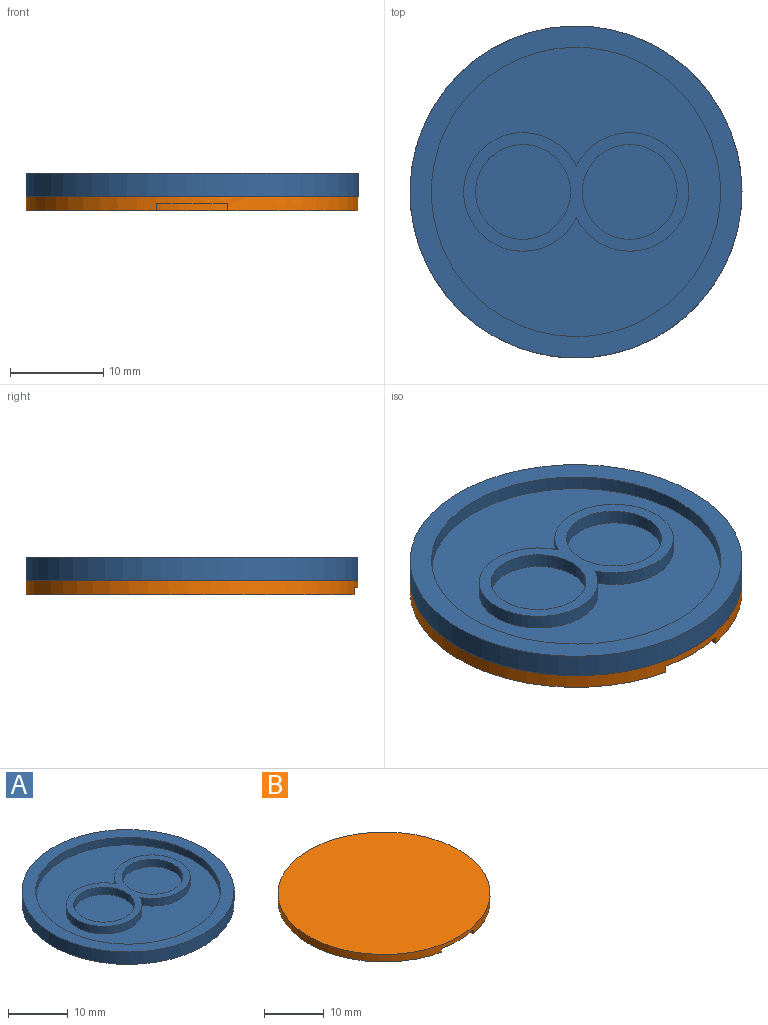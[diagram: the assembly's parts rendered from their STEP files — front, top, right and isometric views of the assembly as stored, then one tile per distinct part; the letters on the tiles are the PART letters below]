
ASSEMBLY  parts=2 mates=1
PART A: 12 faces, bbox 35.6x35.6x2.5 mm
  f0: cylinder r=17.78mm len=35.56mm, axis (0,0,-1), area 283.8mm2, adj f1,f2
  f1: plane 35.56x35.56mm, normal (0,0,1), area 239mm2, adj f0,f3
  f2: plane 35.56x35.56mm, normal (0,0,-1), area 993.1mm2, adj f0
  f3: cylinder r=15.49mm len=30.99mm, axis (0,0,1), area 148.4mm2, adj f1,f4
  f4: plane 30.99x30.99mm, normal (0,0,1), area 505.6mm2, adj f3,f6,f7
  f5: plane 24.13x12.7mm, normal (0,0,1), area 86.5mm2, adj f6,f7,f8,f9
  f6: cylinder r=6.35mm len=12.7mm, axis (0,0,1), area 52.1mm2, adj f4,f5,f7
  f7: cylinder r=6.35mm len=12.7mm, axis (0,0,1), area 52.1mm2, adj f4,f5,f6
  f8: cylinder r=5.08mm len=10.16mm, axis (0,0,1), area 48.6mm2, adj f5,f10
  f9: cylinder r=5.08mm len=10.16mm, axis (0,0,1), area 48.6mm2, adj f5,f11
  f10: plane 10.16x10.16mm, normal (0,0,1), area 81.1mm2, adj f8
  f11: plane 10.16x10.16mm, normal (0,0,1), area 81.1mm2, adj f9
PART B: 170 faces, bbox 35.6x35.6x1.5 mm
  f0: plane 30.99x30.99mm, normal (0,0,-1), area 549.6mm2, adj f4,f5,f6,f7,f8,f9,f10,f11
  f1: plane 35.56x35.15mm, normal (0,0,-1), area 175mm2, adj f2,f165,f167,f169
  f2: cylinder r=17.78mm len=35.56mm, axis (0,0,-1), area 164.4mm2, adj f1,f3,f165,f167,f168
  f3: plane 35.56x35.56mm, normal (0,0,1), area 993.1mm2, adj f2
  f4: plane 1.49x0.76mm, normal (0,-1,0), area 1.1mm2, adj f0,f5,f15,f16
  f5: plane 7.05x0.76mm, normal (-1,0,0), area 5.4mm2, adj f0,f4,f6,f16
  f6: plane 1.49x0.76mm, normal (0,1,0), area 1.1mm2, adj f0,f5,f7,f16
  f7: plane 2.76x0.76mm, normal (1,0,0), area 2.1mm2, adj f0,f6,f8,f16
  f8: plane 2.79x0.76mm, normal (0,1,0), area 2.1mm2, adj f0,f7,f9,f16
  f9: plane 2.76x0.76mm, normal (-1,0,0), area 2.1mm2, adj f0,f8,f10,f16
  f10: plane 1.5x0.76mm, normal (0,1,0), area 1.1mm2, adj f0,f9,f11,f16
  f11: plane 7.05x0.76mm, normal (1,0,0), area 5.4mm2, adj f0,f10,f12,f16
  f12: plane 1.5x0.76mm, normal (0,-1,0), area 1.1mm2, adj f0,f11,f13,f16
  f13: plane 3.04x0.76mm, normal (-1,0,0), area 2.3mm2, adj f0,f12,f14,f16
  f14: plane 2.79x0.76mm, normal (0,-1,0), area 2.1mm2, adj f0,f13,f15,f16
  f15: plane 3.04x0.76mm, normal (1,0,0), area 2.3mm2, adj f0,f4,f14,f16
  f16: plane 7.05x5.78mm, normal (0,0,-1), area 24.5mm2, adj f4,f5,f6,f7,f8,f9,f10,f11
  f17: plane 7.05x0.76mm, normal (-1,0,0), area 5.4mm2, adj f0,f18,f41,f42
  f18: plane 2.19x0.76mm, normal (0,1,0), area 1.7mm2, adj f0,f17,f19,f42
  f19: extruded ~2.18x0.76mm, area 1.7mm2, adj f0,f18,f20,f42
  f20: extruded ~1.36x0.76mm, area 1.2mm2, adj f0,f19,f21,f42
  f21: extruded ~1.04x0.76mm, area 0.8mm2, adj f0,f20,f22,f42
  f22: extruded ~0.79x0.76mm, area 0.7mm2, adj f0,f21,f23,f42
  f23: plane 0.76x0.05mm, normal (1,0,0), area 0mm2, adj f0,f22,f24,f42
  f24: extruded ~0.97x0.76mm, area 0.9mm2, adj f0,f23,f25,f42
  f25: extruded ~1.09x0.76mm, area 0.9mm2, adj f0,f24,f26,f42
  f26: extruded ~1.51x0.76mm, area 1.3mm2, adj f0,f25,f27,f42
  f27: extruded ~1.89x0.76mm, area 1.5mm2, adj f0,f26,f41,f42
  f28: plane 0.93x0.76mm, normal (0,-1,0), area 0.7mm2, adj f29,f39,f42,f44
  f29: plane 1.84x0.76mm, normal (1,0,0), area 1.4mm2, adj f28,f30,f42,f44
  f30: plane 0.97x0.76mm, normal (0,1,0), area 0.7mm2, adj f29,f31,f42,f44
  f31: extruded ~0.91x0.76mm, area 0.7mm2, adj f30,f32,f42,f44
  f32: extruded ~0.76x0.72mm, area 0.6mm2, adj f31,f39,f42,f44
  f33: plane 1.57x0.76mm, normal (1,0,0), area 1.2mm2, adj f34,f40,f42,f43
  f34: plane 0.87x0.76mm, normal (0,1,0), area 0.7mm2, adj f33,f35,f42,f43
  f35: extruded ~0.88x0.76mm, area 0.7mm2, adj f34,f36,f42,f43
  f36: extruded ~0.76x0.62mm, area 0.5mm2, adj f35,f37,f42,f43
  f37: extruded ~0.76x0.58mm, area 0.5mm2, adj f36,f38,f42,f43
  f38: extruded ~0.94x0.76mm, area 0.7mm2, adj f37,f40,f42,f43
  f39: extruded ~1.25x0.88mm, area 1.3mm2, adj f28,f32,f42,f44
  f40: plane 0.79x0.76mm, normal (0,-1,0), area 0.6mm2, adj f33,f38,f42,f43
  f41: plane 2.64x0.76mm, normal (0,-1,0), area 2mm2, adj f0,f17,f27,f42
  f42: plane 7.05x5.23mm, normal (0,0,-1), area 27.1mm2, adj f17,f18,f19,f20,f21,f22,f23,f24
  f43: plane 2.02x1.57mm, normal (0,0,-1), area 2.9mm2, adj f33,f34,f35,f36,f37,f38,f40
  f44: plane 2.18x1.84mm, normal (0,0,-1), area 3.6mm2, adj f28,f29,f30,f31,f32,f39
  f45: extruded ~2.44x2.09mm, area 2.8mm2, adj f0,f46,f52,f53
  f46: extruded ~2.44x2.09mm, area 2.8mm2, adj f0,f45,f47,f53
  f47: extruded ~2.41x2.09mm, area 2.7mm2, adj f0,f46,f52,f53
  f48: extruded ~1.63x1.14mm, area 1.7mm2, adj f49,f51,f53,f54
  f49: extruded ~1.63x1.14mm, area 1.7mm2, adj f48,f50,f53,f54
  f50: extruded ~1.6x1.14mm, area 1.7mm2, adj f49,f51,f53,f54
  f51: extruded ~1.6x1.14mm, area 1.7mm2, adj f48,f50,f53,f54
  f52: extruded ~2.41x2.09mm, area 2.7mm2, adj f0,f45,f47,f53
  f53: plane 4.85x4.18mm, normal (0,0,-1), area 10.4mm2, adj f45,f46,f47,f48,f49,f50,f51,f52
  f54: plane 3.24x2.27mm, normal (0,0,-1), area 6mm2, adj f48,f49,f50,f51
  f55: extruded ~1.45x0.82mm, area 1.3mm2, adj f0,f56,f62,f63
  f56: extruded ~1.6x1.45mm, area 1.9mm2, adj f0,f55,f57,f63
  f57: plane 3.16x0.76mm, normal (-1,0,0), area 2.4mm2, adj f0,f56,f58,f63
  f58: plane 0.93x0.76mm, normal (0,1,0), area 0.7mm2, adj f0,f57,f59,f63
  f59: plane 3.09x0.76mm, normal (1,0,0), area 2.4mm2, adj f0,f58,f60,f63
  f60: extruded ~0.86x0.76mm, area 0.9mm2, adj f0,f59,f61,f63
  f61: extruded ~0.76x0.69mm, area 0.7mm2, adj f0,f60,f62,f63
  f62: plane 0.76x0.64mm, normal (0.59,0.81,0), area 0.6mm2, adj f0,f55,f61,f63
  f63: plane 4.76x2.9mm, normal (0,0,-1), area 5.6mm2, adj f55,f56,f57,f58,f59,f60,f61,f62
  f64: extruded ~2.19x1.82mm, area 2.5mm2, adj f0,f65,f73,f74
  f65: extruded ~2.19x1.81mm, area 2.5mm2, adj f0,f64,f66,f74
  f66: plane 2.57x0.76mm, normal (-1,0,0), area 2mm2, adj f0,f65,f67,f74
  f67: plane 0.9x0.76mm, normal (0,1,0), area 0.7mm2, adj f0,f66,f68,f74
  f68: plane 2.65x0.76mm, normal (1,0,0), area 2mm2, adj f0,f67,f69,f74
  f69: extruded ~1.3x0.91mm, area 1.4mm2, adj f0,f68,f70,f74
  f70: extruded ~1.3x0.88mm, area 1.4mm2, adj f0,f69,f71,f74
  f71: plane 2.65x0.76mm, normal (-1,0,0), area 2mm2, adj f0,f70,f72,f74
  f72: plane 0.93x0.76mm, normal (0,1,0), area 0.7mm2, adj f0,f71,f73,f74
  f73: plane 2.57x0.76mm, normal (1,0,0), area 2mm2, adj f0,f64,f72,f74
  f74: plane 4.76x3.62mm, normal (0,0,-1), area 9.2mm2, adj f64,f65,f66,f67,f68,f69,f70,f71
  f75: plane 4.67x0.76mm, normal (1,0,0), area 3.6mm2, adj f0,f76,f90,f91
  f76: plane 0.88x0.76mm, normal (0,-1,0), area 0.7mm2, adj f0,f75,f77,f91
  f77: plane 1.88x0.76mm, normal (-1,0,0), area 1.4mm2, adj f0,f76,f78,f91
  f78: extruded ~1.63x0.76mm, area 1.2mm2, adj f0,f77,f79,f91
  f79: plane 0.76x0.03mm, normal (0,-1,0), area 0mm2, adj f0,f78,f80,f91
  f80: plane 1x0.76mm, normal (0.9,-0.43,0), area 0.8mm2, adj f0,f79,f81,f91
  f81: plane 2.5x1.35mm, normal (0.88,-0.48,0), area 2.2mm2, adj f0,f80,f82,f91
  f82: plane 0.95x0.76mm, normal (0,-1,0), area 0.7mm2, adj f0,f81,f83,f91
  f83: plane 4.67x0.76mm, normal (-1,0,0), area 3.6mm2, adj f0,f82,f84,f91
  f84: plane 0.88x0.76mm, normal (0,1,0), area 0.7mm2, adj f0,f83,f85,f91
  f85: plane 1.86x0.76mm, normal (1,0,0), area 1.4mm2, adj f0,f84,f86,f91
  f86: extruded ~1.64x0.76mm, area 1.3mm2, adj f0,f85,f87,f91
  f87: plane 0.76x0.03mm, normal (0,1,0), area 0mm2, adj f0,f86,f88,f91
  f88: plane 1.01x0.76mm, normal (-0.91,0.42,0), area 0.8mm2, adj f0,f87,f89,f91
  f89: plane 2.49x1.36mm, normal (-0.88,0.48,0), area 2.2mm2, adj f0,f88,f90,f91
  f90: plane 0.95x0.76mm, normal (0,1,0), area 0.7mm2, adj f0,f75,f89,f91
  f91: plane 4.67x3.57mm, normal (0,0,-1), area 10.9mm2, adj f75,f76,f77,f78,f79,f80,f81,f82
  f92: plane 2.41x1.31mm, normal (0.88,0.48,0), area 2.1mm2, adj f0,f93,f109,f110
  f93: plane 0.99x0.76mm, normal (0,-1,0), area 0.8mm2, adj f0,f92,f94,f110
  f94: plane 1.04x0.76mm, normal (-0.9,-0.43,0), area 0.9mm2, adj f0,f93,f95,f110
  f95: extruded ~0.77x0.76mm, area 0.6mm2, adj f0,f94,f96,f110
  f96: plane 0.76x0.02mm, normal (0,-1,0), area 0mm2, adj f0,f95,f97,f110
  f97: extruded ~0.77x0.76mm, area 0.6mm2, adj f0,f96,f98,f110
  f98: plane 1.04x0.76mm, normal (0.89,-0.45,0), area 0.9mm2, adj f0,f97,f99,f110
  f99: plane 1.04x0.76mm, normal (0,-1,0), area 0.8mm2, adj f0,f98,f100,f110
  f100: plane 2.37x1.31mm, normal (-0.87,0.48,0), area 2.1mm2, adj f0,f99,f101,f110
  f101: plane 2.3x1.23mm, normal (-0.88,-0.47,0), area 2mm2, adj f0,f100,f102,f110
  f102: plane 0.98x0.76mm, normal (0,1,0), area 0.8mm2, adj f0,f101,f103,f110
  f103: plane 0.96x0.76mm, normal (0.91,0.42,0), area 0.8mm2, adj f0,f102,f104,f110
  f104: extruded ~0.76x0.74mm, area 0.6mm2, adj f0,f103,f105,f110
  f105: plane 0.76x0.03mm, normal (0,1,0), area 0mm2, adj f0,f104,f106,f110
  f106: extruded ~0.76x0.74mm, area 0.6mm2, adj f0,f105,f107,f110
  f107: plane 0.96x0.76mm, normal (-0.9,0.44,0), area 0.8mm2, adj f0,f106,f108,f110
  f108: plane 1.04x0.76mm, normal (0,1,0), area 0.8mm2, adj f0,f107,f109,f110
  f109: plane 2.26x1.23mm, normal (0.88,-0.48,0), area 2mm2, adj f0,f92,f108,f110
  f110: plane 4.67x3.78mm, normal (0,0,-1), area 8.4mm2, adj f92,f93,f94,f95,f96,f97,f98,f99
  f111: plane 4.67x0.76mm, normal (1,0,0), area 3.6mm2, adj f0,f112,f114,f115
  f112: plane 0.94x0.76mm, normal (0,-1,0), area 0.7mm2, adj f0,f111,f113,f115
  f113: plane 4.67x0.76mm, normal (-1,0,0), area 3.6mm2, adj f0,f112,f114,f115
  f114: plane 0.94x0.76mm, normal (0,1,0), area 0.7mm2, adj f0,f111,f113,f115
  f115: plane 4.67x0.94mm, normal (0,0,-1), area 4.4mm2, adj f111,f112,f113,f114
  f116: plane 4.67x0.76mm, normal (1,0,0), area 3.6mm2, adj f0,f117,f131,f132
  f117: plane 0.88x0.76mm, normal (0,-1,0), area 0.7mm2, adj f0,f116,f118,f132
  f118: plane 1.88x0.76mm, normal (-1,0,0), area 1.4mm2, adj f0,f117,f119,f132
  f119: extruded ~1.63x0.76mm, area 1.2mm2, adj f0,f118,f120,f132
  f120: plane 0.76x0.03mm, normal (0,-1,0), area 0mm2, adj f0,f119,f121,f132
  f121: plane 1x0.76mm, normal (0.9,-0.43,0), area 0.8mm2, adj f0,f120,f122,f132
  f122: plane 2.5x1.35mm, normal (0.88,-0.48,0), area 2.2mm2, adj f0,f121,f123,f132
  f123: plane 0.95x0.76mm, normal (0,-1,0), area 0.7mm2, adj f0,f122,f124,f132
  f124: plane 4.67x0.76mm, normal (-1,0,0), area 3.6mm2, adj f0,f123,f125,f132
  f125: plane 0.88x0.76mm, normal (0,1,0), area 0.7mm2, adj f0,f124,f126,f132
  f126: plane 1.86x0.76mm, normal (1,0,0), area 1.4mm2, adj f0,f125,f127,f132
  f127: extruded ~1.64x0.76mm, area 1.3mm2, adj f0,f126,f128,f132
  f128: plane 0.76x0.03mm, normal (0,1,0), area 0mm2, adj f0,f127,f129,f132
  f129: plane 1.01x0.76mm, normal (-0.91,0.42,0), area 0.8mm2, adj f0,f128,f130,f132
  f130: plane 2.49x1.36mm, normal (-0.88,0.48,0), area 2.2mm2, adj f0,f129,f131,f132
  f131: plane 0.95x0.76mm, normal (0,1,0), area 0.7mm2, adj f0,f116,f130,f132
  f132: plane 4.67x3.57mm, normal (0,0,-1), area 10.9mm2, adj f116,f117,f118,f119,f120,f121,f122,f123
  f133: extruded ~1.78x0.76mm, area 1.4mm2, adj f134,f146,f147,f163
  f134: extruded ~1.78x0.76mm, area 1.4mm2, adj f133,f135,f147,f163
  f135: extruded ~1.35x0.76mm, area 1.2mm2, adj f134,f136,f147,f163
  f136: extruded ~2.38x1.78mm, area 2.6mm2, adj f135,f137,f147,f163
  f137: extruded ~2.38x1.79mm, area 2.6mm2, adj f136,f146,f147,f163
  f138: extruded ~2.69x0.87mm, area 2.2mm2, adj f0,f139,f145,f147
  f139: extruded ~2.69x0.86mm, area 2.2mm2, adj f0,f138,f140,f147
  f140: extruded ~2.49x0.94mm, area 2.1mm2, adj f0,f139,f141,f147
  f141: extruded ~2.5x0.93mm, area 2.1mm2, adj f0,f140,f142,f147
  f142: extruded ~2.69x0.87mm, area 2.2mm2, adj f0,f141,f143,f147
  f143: extruded ~2.7x0.87mm, area 2.2mm2, adj f0,f142,f144,f147
  f144: extruded ~2.49x0.94mm, area 2.1mm2, adj f0,f143,f145,f147
  f145: extruded ~2.49x0.94mm, area 2.1mm2, adj f0,f138,f144,f147
  f146: extruded ~1.34x0.76mm, area 1.2mm2, adj f133,f137,f147,f163
  f147: plane 7.26x6.71mm, normal (0,0,-1), area 26mm2, adj f133,f134,f135,f136,f137,f138,f139,f140
  f148: extruded ~1.78x0.76mm, area 1.4mm2, adj f149,f161,f162,f164
  f149: extruded ~1.78x0.76mm, area 1.4mm2, adj f148,f150,f162,f164
  f150: extruded ~1.35x0.76mm, area 1.2mm2, adj f149,f151,f162,f164
  f151: extruded ~2.38x1.78mm, area 2.6mm2, adj f150,f152,f162,f164
  f152: extruded ~2.38x1.79mm, area 2.6mm2, adj f151,f161,f162,f164
  f153: extruded ~2.69x0.87mm, area 2.2mm2, adj f0,f154,f160,f162
  f154: extruded ~2.69x0.86mm, area 2.2mm2, adj f0,f153,f155,f162
  f155: extruded ~2.49x0.94mm, area 2.1mm2, adj f0,f154,f156,f162
  f156: extruded ~2.5x0.93mm, area 2.1mm2, adj f0,f155,f157,f162
  f157: extruded ~2.69x0.87mm, area 2.2mm2, adj f0,f156,f158,f162
  f158: extruded ~2.7x0.87mm, area 2.2mm2, adj f0,f157,f159,f162
  f159: extruded ~2.49x0.94mm, area 2.1mm2, adj f0,f158,f160,f162
  f160: extruded ~2.49x0.94mm, area 2.1mm2, adj f0,f153,f159,f162
  f161: extruded ~1.34x0.76mm, area 1.2mm2, adj f148,f152,f162,f164
  f162: plane 7.26x6.71mm, normal (0,0,-1), area 26mm2, adj f148,f149,f150,f151,f152,f153,f154,f155
  f163: plane 4.76x3.58mm, normal (0,0,-1), area 14.2mm2, adj f133,f134,f135,f136,f137,f146
  f164: plane 4.76x3.58mm, normal (0,0,-1), area 14.2mm2, adj f148,f149,f150,f151,f152,f161
  f165: plane 1.83x0.76mm, normal (1,0,0), area 1.4mm2, adj f1,f2,f168,f169
  f166: cylinder r=15.49mm len=30.99mm, axis (0,0,-1), area 74.2mm2, adj f0,f168
  f167: plane 1.83x0.76mm, normal (-1,0,0), area 1.4mm2, adj f1,f2,f168,f169
  f168: plane 33.78x32mm, normal (0,0,-1), area 63.9mm2, adj f2,f165,f166,f167,f169
  f169: cylinder r=16mm len=32mm, axis (0,0,-1), area 70.8mm2, adj f1,f165,f167,f168
PLACE A t=(-6.45,-25.08,-32.14)mm fixed
PLACE B t=(-6.45,-25.08,-33.67)mm
MATE fastened B.f2 <-> A.f0  axis (0,0,1) through (-6.45,-25.08,-32.14)mm
